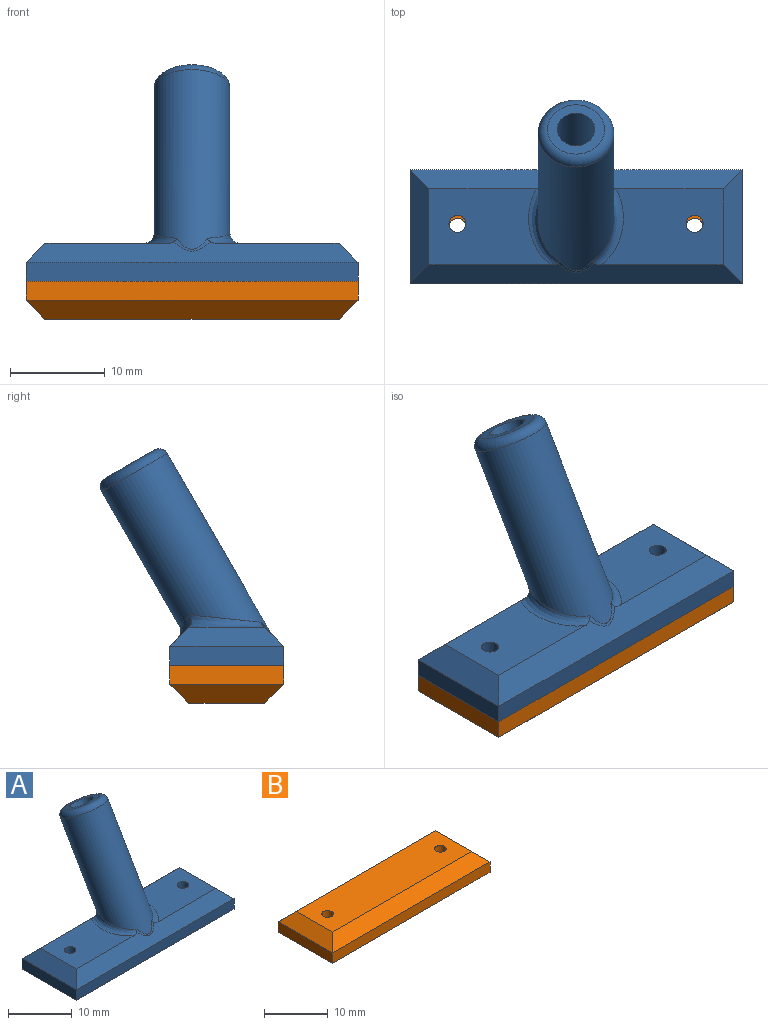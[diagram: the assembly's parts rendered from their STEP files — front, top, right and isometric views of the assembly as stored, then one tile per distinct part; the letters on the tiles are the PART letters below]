
ASSEMBLY  parts=2 mates=1
PART A: 23 faces, bbox 35.1x19.7x23 mm
  f0: plane 12.84x8mm, normal (0,0,1), area 85.6mm2, adj f11,f13,f15,f16,f18
  f1: plane 12.84x8mm, normal (0,0,1), area 85.6mm2, adj f12,f13,f14,f16,f19
  f2: plane 35x2mm, normal (0,-1,0), area 70mm2, adj f3,f5,f6,f13
  f3: plane 12x2mm, normal (1,0,0), area 24mm2, adj f2,f4,f6,f14
  f4: plane 35x2mm, normal (0,1,0), area 70mm2, adj f3,f5,f6,f16
  f5: plane 12x2mm, normal (-1,0,0), area 24mm2, adj f2,f4,f6,f15
  f6: plane 35x12mm, normal (0,0,-1), area 414.9mm2, adj f2,f3,f4,f5,f11,f12
  f7: cylinder r=2mm len=18.69mm, axis (0,-0.5,-0.87), area 242.1mm2, adj f9,f21
  f8: cylinder r=4mm len=21.62mm, axis (0,-0.5,-0.87), area 446.8mm2, adj f17,f18,f19,f20,f22
  f9: plane 6x5.2mm, normal (0,0.5,0.87), area 15.7mm2, adj f7,f22
  f10: plane 2.31x2mm, normal (0,0,1), area 3.6mm2, adj f21
  f11: cylinder r=0.9mm len=4mm, axis (0,0,1), area 22.6mm2, adj f0,f6
  f12: cylinder r=0.9mm len=4mm, axis (0,0,1), area 22.6mm2, adj f1,f6
  f13: plane 35.11x2.28mm, normal (0,-0.71,0.71), area 90.8mm2, adj f0,f1,f2,f14,f15,f18,f19,f20
  f14: plane 12x2mm, normal (0.71,0,0.71), area 28.3mm2, adj f1,f3,f13,f16
  f15: plane 12x2mm, normal (-0.71,0,0.71), area 28.3mm2, adj f0,f5,f13,f16
  f16: plane 35.06x2.17mm, normal (0,0.71,0.71), area 85.4mm2, adj f0,f1,f4,f14,f15,f17,f18,f19
  f17: bspline ~7.92x2.44mm, area 10.4mm2, adj f8,f16,f18,f19
  f18: bspline ~8.83x3.42mm, area 12.6mm2, adj f0,f8,f13,f16,f17,f20
  f19: bspline ~8.83x3.42mm, area 12.6mm2, adj f1,f8,f13,f16,f17,f20
  f20: bspline ~3.96x1.36mm, area 1.7mm2, adj f8,f13,f18,f19
  f21: bspline ~4.16x4mm, area 16.9mm2, adj f7,f10
  f22: torus R=3mm, axis (0,0.5,0.87), area 35.9mm2, adj f8,f9
PART B: 12 faces, bbox 35x12x4 mm
  f0: plane 35x2mm, normal (0,-1,0), area 70mm2, adj f1,f5,f7,f9
  f1: plane 12x2mm, normal (1,0,0), area 24mm2, adj f0,f2,f7,f11
  f2: plane 35x2mm, normal (0,1,0), area 70mm2, adj f1,f5,f7,f10
  f3: cylinder r=0.9mm len=4mm, axis (0,0,-1), area 22.6mm2, adj f6,f7
  f4: cylinder r=0.9mm len=4mm, axis (0,0,-1), area 22.6mm2, adj f6,f7
  f5: plane 12x2mm, normal (-1,0,0), area 24mm2, adj f0,f2,f7,f8
  f6: plane 31x8mm, normal (0,0,1), area 242.9mm2, adj f3,f4,f8,f9,f10,f11
  f7: plane 35x12mm, normal (0,0,-1), area 414.9mm2, adj f0,f1,f2,f3,f4,f5
  f8: plane 12x2mm, normal (-0.71,0,0.71), area 28.3mm2, adj f5,f6,f9,f10
  f9: plane 35x2mm, normal (0,-0.71,0.71), area 93.3mm2, adj f0,f6,f8,f11
  f10: plane 35x2mm, normal (0,0.71,0.71), area 93.3mm2, adj f2,f6,f8,f11
  f11: plane 12x2mm, normal (0.71,0,0.71), area 28.3mm2, adj f1,f6,f9,f10
PLACE A t=(-3.64,4.03,3.28)mm fixed
PLACE B rot(axis=(1,0,0),180deg) t=(-3.64,4.02,3.28)mm
MATE planar A.f6 <-> B.f7  axis (0,0,-1) through (-3.64,4.02,3.28)mm
